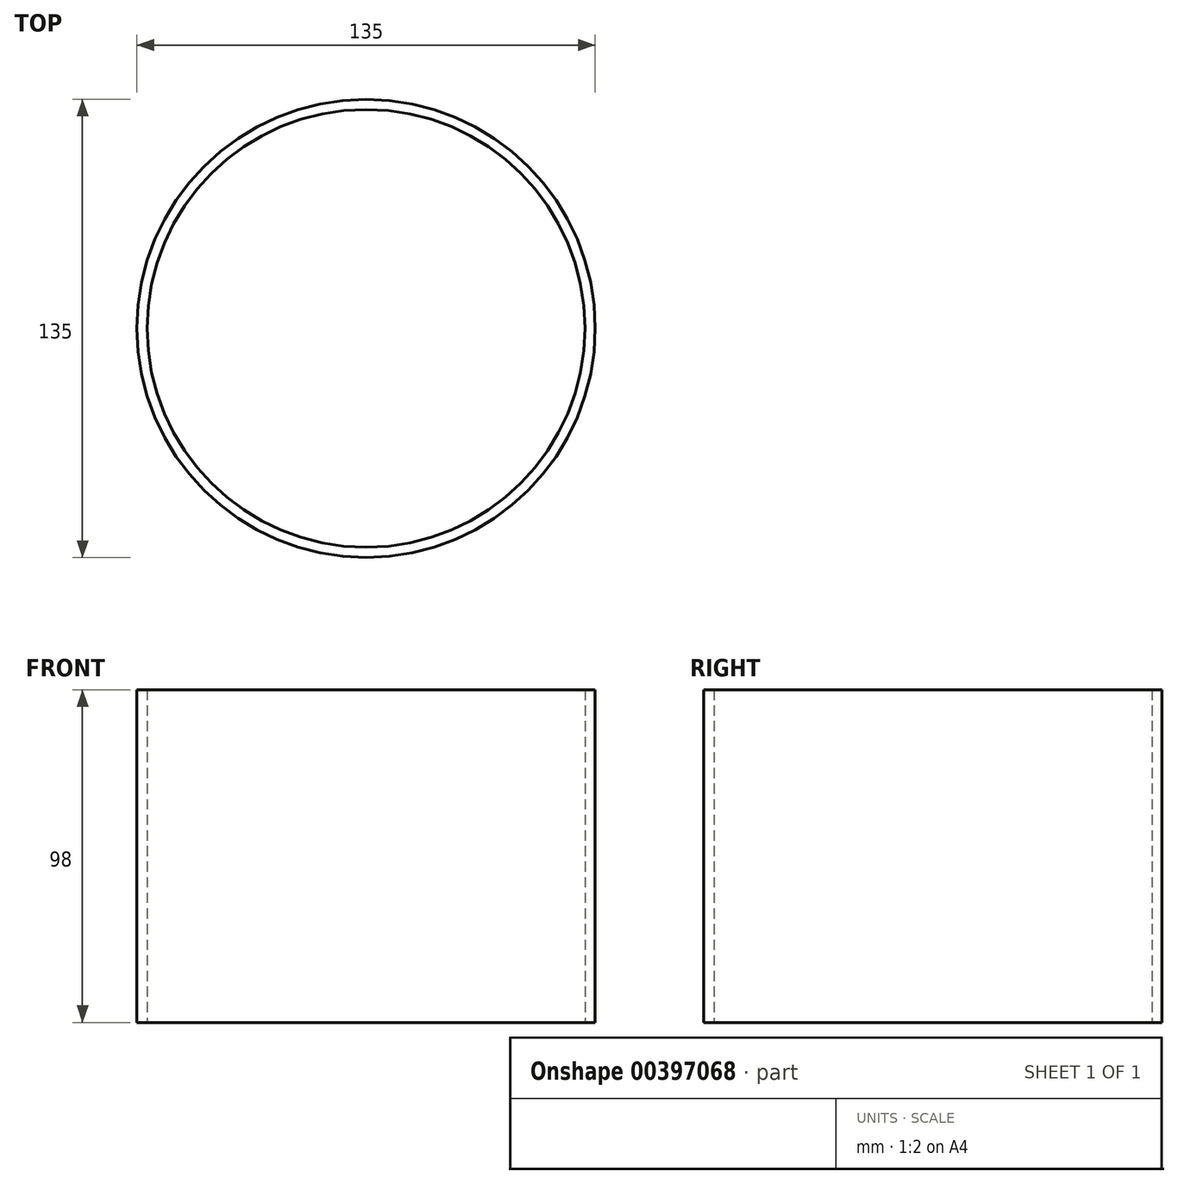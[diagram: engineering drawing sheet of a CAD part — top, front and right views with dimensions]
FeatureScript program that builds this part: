
annotation { "Feature Type Name" : "Feature", "Feature Type Description" : "" }
export const myFeature = defineFeature(function(context is Context, id is Id, definition is map)
    precondition{}
    {
        {
            var Q0;
            Q0=qCreatedBy(makeId("Right.planeOp"),FACE);
            var sketch = newSketch(context, id + "F0", { "sketchPlane" : qUnion([Q0])});
            skLineSegment(sketch, "E0.bottom", {"start": v(67.5, 49) * mm, "end": v(64.5, 49) * mm});
            skLineSegment(sketch, "E0.top", {"start": v(67.5, -49) * mm, "end": v(64.5, -49) * mm});
            skLineSegment(sketch, "E0.left", {"start": v(67.5, 49) * mm, "end": v(67.5, -49) * mm});
            skLineSegment(sketch, "E0.right", {"start": v(-67.5, 49) * mm, "end": v(-67.5, -49) * mm});
            skPoint(sketch, "E0.middle", {"position": v(0, 0) * mm});
            skLineSegment(sketch, "E1", {"start": v(0, -49) * mm, "end": v(0, 49) * mm, "construction": true});
            skLineSegment(sketch, "E2", {"start": v(64.5, 49) * mm, "end": v(64.5, -49) * mm});
            skLineSegment(sketch, "E3.MirrorCS", {"start": v(-64.5, 49) * mm, "end": v(-64.5, -49) * mm});
            skLineSegment(sketch, "E4.trimOffspring", {"start": v(-64.5, 49) * mm, "end": v(-67.5, 49) * mm});
            skLineSegment(sketch, "E5.trimOffspring", {"start": v(-64.5, -49) * mm, "end": v(-67.5, -49) * mm});
            skSolve(sketch);
        }
        {
            var Q0;
            Q0=makeQuery(id+"F0.imprint","IMPRINT",FACE,{"disambiguationData":[TD([[makeQuery(id+"F0.imprint","IMPRINT",EDGE,{"derivedFrom":sQuery(id+"F0.wireOp",EDGE,"E0.bottom")}),1.0]])]});
            var Q1;
            Q1=sQuery(id+"F0.wireOp",EDGE,"E1");
            revolve(context, id + "F1", {"entities" : qUnion([Q0]), "axis" : qUnion([Q1]), "revolveType" : RevolveType.FULL});
        }
    });
